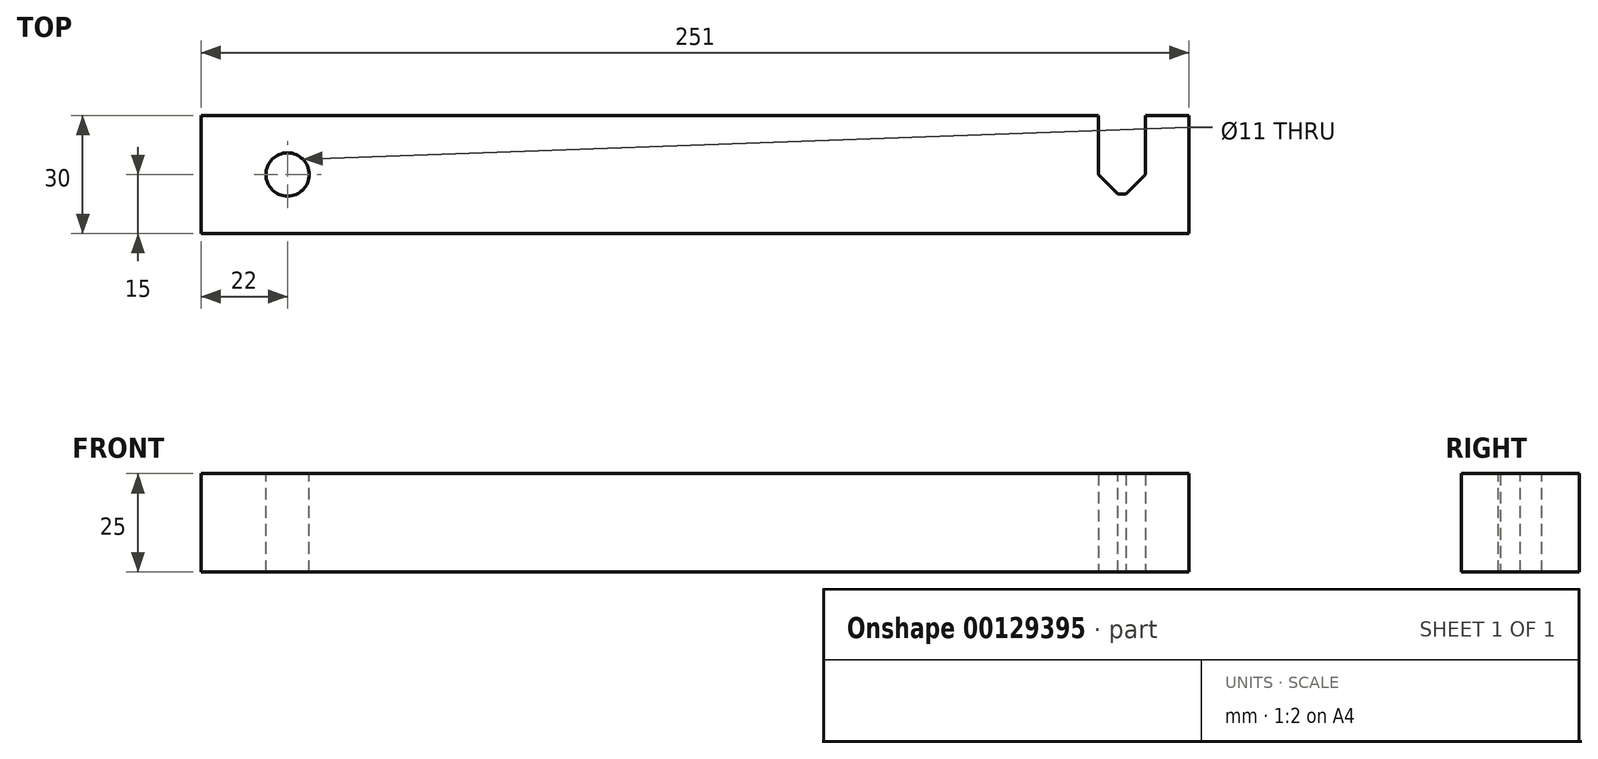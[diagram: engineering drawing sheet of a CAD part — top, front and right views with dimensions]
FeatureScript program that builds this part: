
annotation { "Feature Type Name" : "Feature", "Feature Type Description" : "" }
export const myFeature = defineFeature(function(context is Context, id is Id, definition is map)
    precondition{}
    {
        {
            var Q0;
            Q0=qCreatedBy(makeId("Top.planeOp"),FACE);
            var sketch = newSketch(context, id + "F0", { "sketchPlane" : qUnion([Q0])});
            skLineSegment(sketch, "E0", {"start": v(-125.5, 15) * mm, "end": v(-125.5, -15) * mm});
            skLineSegment(sketch, "E1", {"start": v(-125.5, -15) * mm, "end": v(125.5, -15) * mm});
            skLineSegment(sketch, "E2", {"start": v(125.5, -15) * mm, "end": v(125.5, 15) * mm});
            skLineSegment(sketch, "E3", {"start": v(125.5, 15) * mm, "end": v(114.5, 15) * mm});
            skLineSegment(sketch, "E4", {"start": v(114.5, 15) * mm, "end": v(114.5, -5) * mm});
            skLineSegment(sketch, "E5", {"start": v(114.5, -5) * mm, "end": v(102.5, -5) * mm});
            skLineSegment(sketch, "E6", {"start": v(102.5, -5) * mm, "end": v(102.5, 15) * mm});
            skLineSegment(sketch, "E7", {"start": v(102.5, 15) * mm, "end": v(-125.5, 15) * mm});
            skLineSegment(sketch, "E8", {"start": v(125.5, 0) * mm, "end": v(125.52, 0) * mm, "construction": true});
            skPoint(sketch, "E8.startSnap0", {"position": v(-125.5, 0) * mm});
            skLineSegment(sketch, "E9", {"start": v(0, -15) * mm, "end": v(0, 15) * mm, "construction": true});
            skLineSegment(sketch, "E10", {"start": v(-125.5, 0) * mm, "end": v(0, 0) * mm, "construction": true});
            skSolve(sketch);
        }
        {
            var Q0;
            Q0 = qSketchRegion(id + "F0", true);
            extrude(context, id + "F1", {"entities" : qUnion([Q0]), "endBound" : BoundingType.SYMMETRIC, "depth" : 25 * mm});
        }
        {
            var Q0;
            Q0=makeQuery(id+"F1.opExtrude","CAP_FACE",FACE,{"disambiguationData":[OSD([sQuery(id+"F0.wireOp",EDGE,"E0"),sQuery(id+"F0.wireOp",EDGE,"E1"),sQuery(id+"F0.wireOp",EDGE,"E2"),sQuery(id+"F0.wireOp",EDGE,"E3"),sQuery(id+"F0.wireOp",EDGE,"E4"),sQuery(id+"F0.wireOp",EDGE,"E5"),sQuery(id+"F0.wireOp",EDGE,"E6"),sQuery(id+"F0.wireOp",EDGE,"E7")])],"isStart":false});
            var sketch = newSketch(context, id + "F2", { "sketchPlane" : qUnion([Q0])});
            skCircle(sketch, "E11", {"center": v(-103.5, 0) * mm, "radius": 5.5 * mm});
            skSolve(sketch);
        }
        {
            var Q0;
            Q0=makeQuery(id+"F2.imprint","IMPRINT",FACE,{"disambiguationData":[TD([[makeQuery(id+"F2.imprint","IMPRINT",EDGE,{"derivedFrom":sQuery(id+"F2.wireOp",EDGE,"E11")}),1.0]])]});
            var Q1;
            Q1=sQuery(id+"F2.wireOp",EDGE,"E11");
            extrude(context, id + "F3", {"entities" : qUnion([Q0]), "operationType" : NewBodyOperationType.REMOVE, "surfaceEntities" : qUnion([Q1]), "endBound" : BoundingType.THROUGH_ALL, "oppositeDirection" : true, "depth" : 25 * mm});
        }
        {
            var Q0;
            Q0=makeQuery(id+"F1.opExtrude","SWEPT_EDGE",EDGE,{"disambiguationData":[OSD([sQuery(id+"F0.wireOp",EDGE,"E5"),sQuery(id+"F0.wireOp",EDGE,"E6")])]});
            var Q1;
            Q1=makeQuery(id+"F1.opExtrude","SWEPT_EDGE",EDGE,{"disambiguationData":[OSD([sQuery(id+"F0.wireOp",EDGE,"E4"),sQuery(id+"F0.wireOp",EDGE,"E5")])]});
            chamfer(context, id + "F4", {"entities" : qUnion([Q0, Q1]), "width" : 5 * mm, "tangentPropagation" : true});
        }
    });
